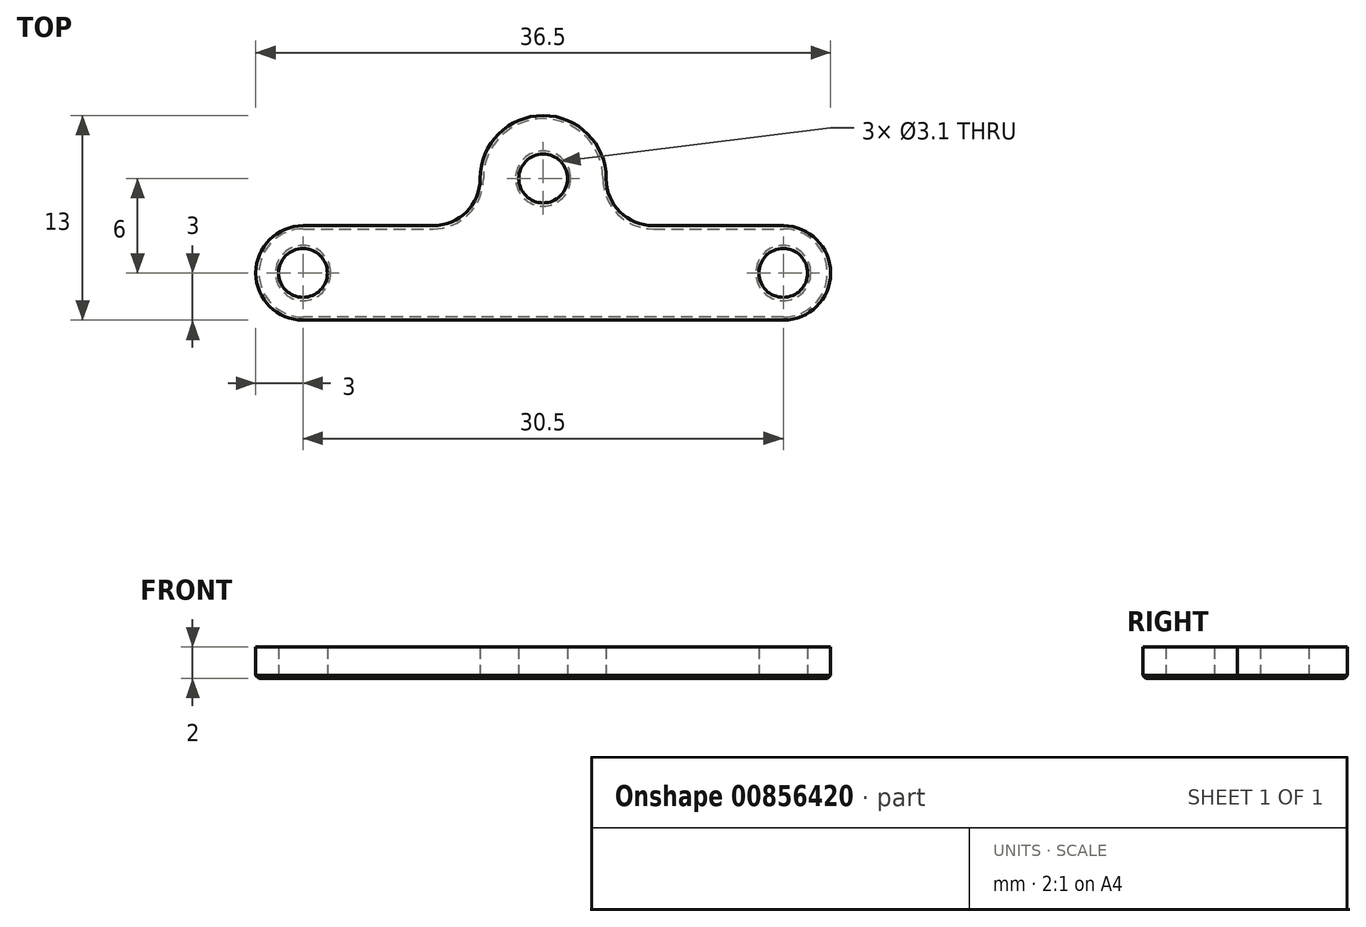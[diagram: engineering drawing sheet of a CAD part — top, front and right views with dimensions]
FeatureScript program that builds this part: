
annotation { "Feature Type Name" : "Feature", "Feature Type Description" : "" }
export const myFeature = defineFeature(function(context is Context, id is Id, definition is map)
    precondition{}
    {
        {
            var Q0;
            Q0=qCreatedBy(makeId("Top.planeOp"),FACE);
            var sketch = newSketch(context, id + "F0", { "sketchPlane" : qUnion([Q0])});
            skCircle(sketch, "E0", {"center": v(-15.25, 0) * mm, "radius": 1.55 * mm});
            skCircle(sketch, "E1.MirrorC", {"center": v(15.25, 0) * mm, "radius": 1.55 * mm});
            skLineSegment(sketch, "E2", {"start": v(-15.25, 0) * mm, "end": v(15.25, 0) * mm, "construction": true});
            skArc(sketch, "E3.0.startCap", {"start": v(-15.25, -3) * mm, "mid": v(-18.25, 0) * mm, "end": v(-15.25, 3) * mm});
            skArc(sketch, "E3.0.endCap", {"start": v(15.25, 3) * mm, "mid": v(18.25, 0) * mm, "end": v(15.25, -3) * mm});
            skLineSegment(sketch, "E3.0.left", {"start": v(-15.25, 3) * mm, "end": v(15.25, 3) * mm});
            skLineSegment(sketch, "E3.0.right", {"start": v(-15.25, -3) * mm, "end": v(15.25, -3) * mm});
            skCircle(sketch, "E4", {"center": v(0, 6) * mm, "radius": 1.55 * mm});
            skArc(sketch, "E5", {"start": v(-4, 6) * mm, "mid": v(0, 10) * mm, "end": v(4, 6) * mm});
            skLineSegment(sketch, "E6", {"start": v(-4, 6) * mm, "end": v(-4, 3) * mm});
            skLineSegment(sketch, "E7", {"start": v(4, 6) * mm, "end": v(4, 3) * mm});
            skSolve(sketch);
        }
        {
            var Q0;
            Q0 = qSketchRegion(id + "F0", true);
            extrude(context, id + "F1", {"entities" : qUnion([Q0]), "depth" : 2 * mm, "offsetDistance" : 25 * mm});
        }
        {
            var Q0;
            Q0=makeQuery(id+"F1.opExtrude","SWEPT_EDGE",EDGE,{"disambiguationData":[OSD([sQuery(id+"F0.wireOp",EDGE,"E3.0.left"),sQuery(id+"F0.wireOp",EDGE,"E7")])]});
            var Q1;
            Q1=makeQuery(id+"F1.opExtrude","SWEPT_EDGE",EDGE,{"disambiguationData":[OSD([sQuery(id+"F0.wireOp",EDGE,"E3.0.left"),sQuery(id+"F0.wireOp",EDGE,"E6")])]});
            fillet(context, id + "F2", {"entities" : qUnion([Q0, Q1]), "radius" : 3 * mm, "allowEdgeOverflow" : false});
        }
        {
            var Q0;
            Q0=makeQuery(id+"F1.opExtrude","CAP_FACE",FACE,{"disambiguationData":[OSD([sQuery(id+"F0.wireOp",EDGE,"E0"),sQuery(id+"F0.wireOp",EDGE,"E1.MirrorC"),sQuery(id+"F0.wireOp",EDGE,"E3.0.startCap"),sQuery(id+"F0.wireOp",EDGE,"E3.0.endCap"),sQuery(id+"F0.wireOp",EDGE,"E3.0.left"),sQuery(id+"F0.wireOp",EDGE,"E3.0.right"),sQuery(id+"F0.wireOp",EDGE,"E4"),sQuery(id+"F0.wireOp",EDGE,"E5"),sQuery(id+"F0.wireOp",EDGE,"E6"),sQuery(id+"F0.wireOp",EDGE,"E7")])],"isStart":true});
            chamfer(context, id + "F3", {"entities" : qUnion([Q0]), "width" : 0.2 * mm});
        }
    });
